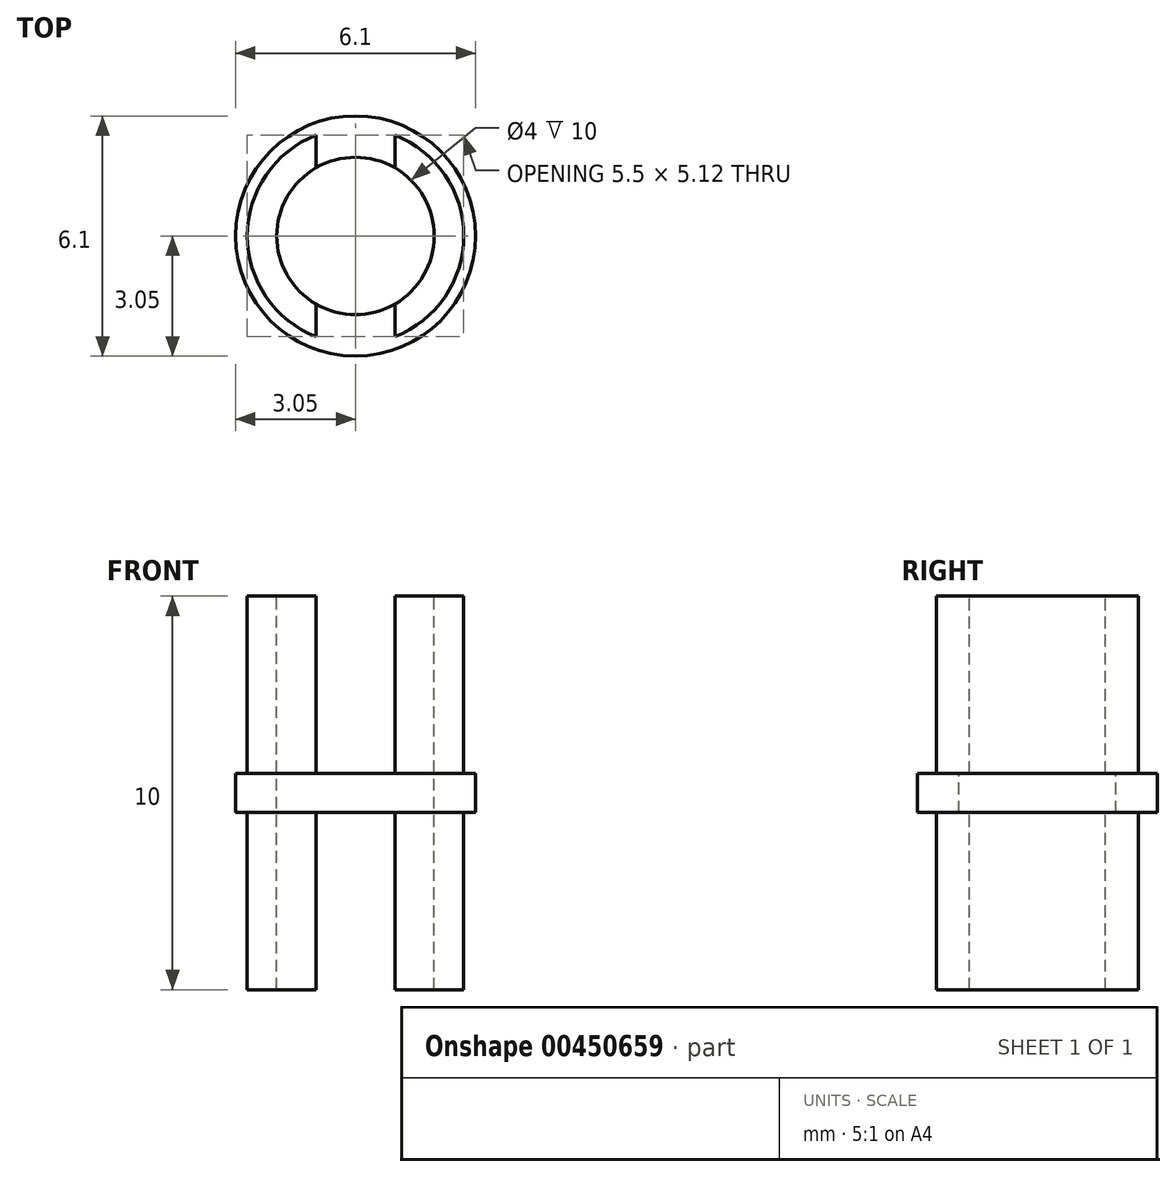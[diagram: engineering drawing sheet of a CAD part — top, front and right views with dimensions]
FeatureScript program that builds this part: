
annotation { "Feature Type Name" : "Feature", "Feature Type Description" : "" }
export const myFeature = defineFeature(function(context is Context, id is Id, definition is map)
    precondition{}
    {
        {
            var Q0;
            Q0=qCreatedBy(makeId("Top.planeOp"),FACE);
            var sketch = newSketch(context, id + "F0", { "sketchPlane" : qUnion([Q0])});
            skCircle(sketch, "E0", {"center": v(0, 0) * mm, "radius": 2.75 * mm});
            skSolve(sketch);
        }
        {
            var Q0;
            Q0 = qSketchRegion(id + "F0", true);
            extrude(context, id + "F1", {"entities" : qUnion([Q0]), "endBound" : BoundingType.SYMMETRIC, "depth" : 10 * mm});
        }
        {
            var Q0;
            Q0=qCreatedBy(makeId("Top.planeOp"),FACE);
            var sketch = newSketch(context, id + "F2", { "sketchPlane" : qUnion([Q0])});
            skCircle(sketch, "E1", {"center": v(0, 0) * mm, "radius": 3.05 * mm});
            skSolve(sketch);
        }
        {
            var Q0;
            Q0 = qSketchRegion(id + "F2", true);
            extrude(context, id + "F3", {"entities" : qUnion([Q0]), "operationType" : NewBodyOperationType.ADD, "endBound" : BoundingType.SYMMETRIC, "depth" : 1 * mm});
        }
        {
            var Q0;
            Q0=makeQuery(id+"F1.opExtrude","CAP_FACE",FACE,{"disambiguationData":[OSD([sQuery(id+"F0.wireOp",EDGE,"E0")])],"isStart":false});
            var sketch = newSketch(context, id + "F4", { "sketchPlane" : qUnion([Q0])});
            skCircle(sketch, "E2", {"center": v(0, 0) * mm, "radius": 2 * mm});
            skSolve(sketch);
        }
        {
            var Q0;
            Q0 = qSketchRegion(id + "F4", true);
            extrude(context, id + "F5", {"entities" : qUnion([Q0]), "operationType" : NewBodyOperationType.REMOVE, "oppositeDirection" : true, "depth" : 25 * mm});
        }
        {
            var Q0;
            Q0=makeQuery(id+"F1.opExtrude","CAP_FACE",FACE,{"disambiguationData":[OSD([sQuery(id+"F0.wireOp",EDGE,"E0")])],"isStart":false});
            var sketch = newSketch(context, id + "F6", { "sketchPlane" : qUnion([Q0])});
            skLineSegment(sketch, "E3.bottom", {"start": v(-1, 3.9) * mm, "end": v(1, 3.9) * mm});
            skLineSegment(sketch, "E3.top", {"start": v(-1, -4.16) * mm, "end": v(1, -4.16) * mm});
            skLineSegment(sketch, "E3.left", {"start": v(-1, 3.9) * mm, "end": v(-1, -4.16) * mm});
            skLineSegment(sketch, "E3.right", {"start": v(1, 3.9) * mm, "end": v(1, -4.16) * mm});
            skSolve(sketch);
        }
        {
            var Q0;
            Q0 = qSketchRegion(id + "F6", true);
            extrude(context, id + "F7", {"entities" : qUnion([Q0]), "operationType" : NewBodyOperationType.REMOVE, "oppositeDirection" : true, "depth" : 4.5 * mm});
        }
        {
            var Q0;
            Q0=makeQuery(id+"F1.opExtrude","CAP_FACE",FACE,{"disambiguationData":[OSD([sQuery(id+"F0.wireOp",EDGE,"E0")])],"isStart":true});
            var sketch = newSketch(context, id + "F8", { "sketchPlane" : qUnion([Q0])});
            skLineSegment(sketch, "E4.bottom", {"start": v(-1, 4.02) * mm, "end": v(1, 4.02) * mm});
            skLineSegment(sketch, "E4.top", {"start": v(-1, -4.02) * mm, "end": v(1, -4.02) * mm});
            skLineSegment(sketch, "E4.left", {"start": v(-1, 4.02) * mm, "end": v(-1, -4.02) * mm});
            skLineSegment(sketch, "E4.right", {"start": v(1, 4.02) * mm, "end": v(1, -4.02) * mm});
            skSolve(sketch);
        }
        {
            var Q0;
            Q0 = qSketchRegion(id + "F8", true);
            extrude(context, id + "F9", {"entities" : qUnion([Q0]), "operationType" : NewBodyOperationType.REMOVE, "oppositeDirection" : true, "depth" : 4.5 * mm});
        }
    });
